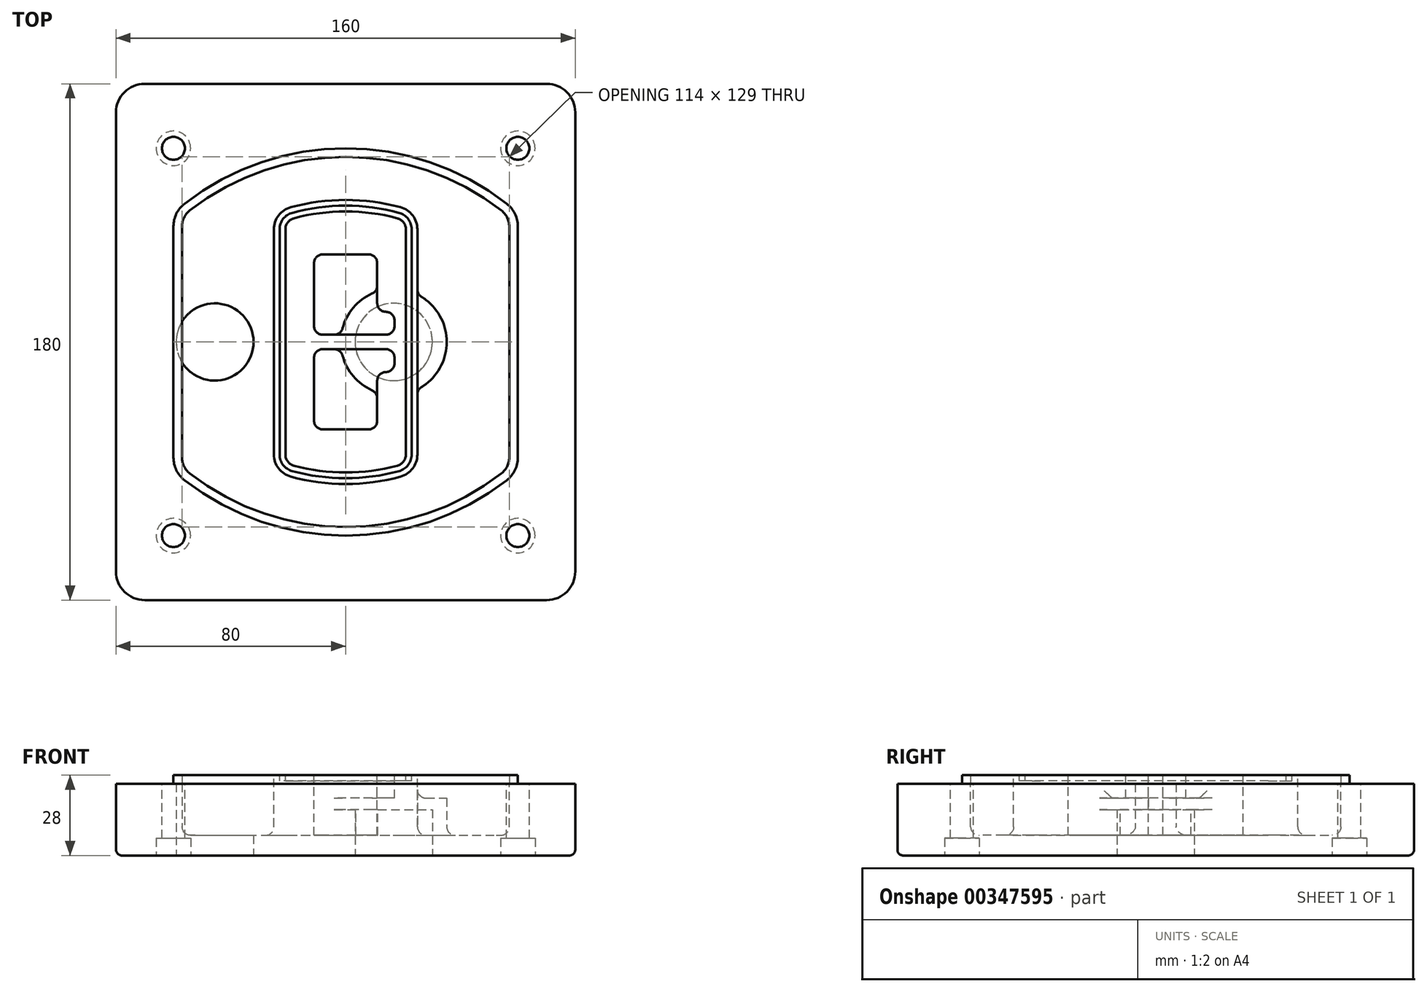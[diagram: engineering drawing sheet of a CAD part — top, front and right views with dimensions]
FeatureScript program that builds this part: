
annotation { "Feature Type Name" : "Feature", "Feature Type Description" : "" }
export const myFeature = defineFeature(function(context is Context, id is Id, definition is map)
    precondition{}
    {
        {
            var Q0;
            Q0=qCreatedBy(makeId("Top.planeOp"),FACE);
            var sketch = newSketch(context, id + "F0", { "sketchPlane" : qUnion([Q0])});
            skPoint(sketch, "E0.rect.middle", {"position": v(0, 0) * mm});
            skLineSegment(sketch, "E1.bottom", {"start": v(-70, -90) * mm, "end": v(70, -90) * mm});
            skLineSegment(sketch, "E1.top", {"start": v(-70, 90) * mm, "end": v(70, 90) * mm});
            skLineSegment(sketch, "E1.left", {"start": v(-80, -80) * mm, "end": v(-80, 80) * mm});
            skLineSegment(sketch, "E1.right", {"start": v(80, -80) * mm, "end": v(80, 80) * mm});
            skLineSegment(sketch, "E2", {"start": v(-80, 90) * mm, "end": v(80, -90) * mm, "construction": true});
            skLineSegment(sketch, "E3", {"start": v(80, 90) * mm, "end": v(-80, -90) * mm, "construction": true});
            skCircle(sketch, "E4", {"center": v(-60, 67.5) * mm, "radius": 4 * mm});
            skCircle(sketch, "E5", {"center": v(60, 67.5) * mm, "radius": 4 * mm});
            skCircle(sketch, "E6", {"center": v(60, -67.5) * mm, "radius": 4 * mm});
            skCircle(sketch, "E7", {"center": v(-60, -67.5) * mm, "radius": 4 * mm});
            skLineSegment(sketch, "E8", {"start": v(-60, 67.5) * mm, "end": v(60, 67.5) * mm, "construction": true});
            skLineSegment(sketch, "E9", {"start": v(60, 67.5) * mm, "end": v(60, -67.5) * mm, "construction": true});
            skLineSegment(sketch, "E10", {"start": v(60, -67.5) * mm, "end": v(-60, -67.5) * mm, "construction": true});
            skLineSegment(sketch, "E11", {"start": v(-60, -67.5) * mm, "end": v(-60, 67.5) * mm, "construction": true});
            skLineSegment(sketch, "E12", {"start": v(-60, 40.3) * mm, "end": v(-60, -40.3) * mm});
            skLineSegment(sketch, "E13", {"start": v(60, 40.3) * mm, "end": v(60, -40.3) * mm});
            skArc(sketch, "E14", {"start": v(56.15, 48.18) * mm, "mid": v(0, 67.5) * mm, "end": v(-56.15, 48.18) * mm});
            skArc(sketch, "E15", {"start": v(-56.15, -48.18) * mm, "mid": v(0, -67.5) * mm, "end": v(56.15, -48.18) * mm});
            skLineSegment(sketch, "E16", {"start": v(-60, 0) * mm, "end": v(60, 0) * mm, "construction": true});
            skPoint(sketch, "E17.visualSharp", {"position": v(-60, -45) * mm});
            skArc(sketch, "E17.filletArc", {"start": v(-60, -40.3) * mm, "mid": v(-58.99, -44.68) * mm, "end": v(-56.15, -48.18) * mm});
            skPoint(sketch, "E18.visualSharp", {"position": v(-60, 45) * mm});
            skArc(sketch, "E18.filletArc", {"start": v(-56.15, 48.18) * mm, "mid": v(-58.99, 44.68) * mm, "end": v(-60, 40.3) * mm});
            skPoint(sketch, "E19.visualSharp", {"position": v(60, 45) * mm});
            skArc(sketch, "E19.filletArc", {"start": v(60, 40.3) * mm, "mid": v(58.99, 44.68) * mm, "end": v(56.15, 48.18) * mm});
            skPoint(sketch, "E20.visualSharp", {"position": v(60, -45) * mm});
            skArc(sketch, "E20.filletArc", {"start": v(56.15, -48.18) * mm, "mid": v(58.99, -44.68) * mm, "end": v(60, -40.3) * mm});
            skPoint(sketch, "E21.visualSharp", {"position": v(-80, 90) * mm});
            skArc(sketch, "E21.filletArc", {"start": v(-70, 90) * mm, "mid": v(-77.07, 87.07) * mm, "end": v(-80, 80) * mm});
            skPoint(sketch, "E22.visualSharp", {"position": v(80, 90) * mm});
            skArc(sketch, "E22.filletArc", {"start": v(80, 80) * mm, "mid": v(77.07, 87.07) * mm, "end": v(70, 90) * mm});
            skPoint(sketch, "E23.visualSharp", {"position": v(80, -90) * mm});
            skArc(sketch, "E23.filletArc", {"start": v(70, -90) * mm, "mid": v(77.07, -87.07) * mm, "end": v(80, -80) * mm});
            skPoint(sketch, "E24.visualSharp", {"position": v(-80, -90) * mm});
            skArc(sketch, "E24.filletArc", {"start": v(-80, -80) * mm, "mid": v(-77.07, -87.07) * mm, "end": v(-70, -90) * mm});
            skArc(sketch, "E25.0", {"start": v(57, 40.3) * mm, "mid": v(56.3, 43.36) * mm, "end": v(54.3, 45.81) * mm});
            skLineSegment(sketch, "E25.1", {"start": v(57, 40.3) * mm, "end": v(57, -40.3) * mm});
            skArc(sketch, "E25.2", {"start": v(54.3, -45.81) * mm, "mid": v(56.3, -43.36) * mm, "end": v(57, -40.3) * mm});
            skArc(sketch, "E25.3", {"start": v(-54.3, -45.81) * mm, "mid": v(0, -64.5) * mm, "end": v(54.3, -45.81) * mm});
            skArc(sketch, "E25.4", {"start": v(-57, -40.3) * mm, "mid": v(-56.3, -43.36) * mm, "end": v(-54.3, -45.81) * mm});
            skArc(sketch, "E25.5", {"start": v(54.3, 45.81) * mm, "mid": v(0, 64.5) * mm, "end": v(-54.3, 45.81) * mm});
            skLineSegment(sketch, "E25.6", {"start": v(-57, 40.3) * mm, "end": v(-57, -40.3) * mm});
            skArc(sketch, "E25.7", {"start": v(-54.3, 45.81) * mm, "mid": v(-56.3, 43.36) * mm, "end": v(-57, 40.3) * mm});
            skArc(sketch, "E26.0", {"start": v(-58.62, 51.33) * mm, "mid": v(-62.58, 46.43) * mm, "end": v(-64, 40.3) * mm});
            skArc(sketch, "E26.1", {"start": v(58.62, 51.33) * mm, "mid": v(0, 71.5) * mm, "end": v(-58.62, 51.33) * mm});
            skArc(sketch, "E26.2", {"start": v(64, 40.3) * mm, "mid": v(62.58, 46.43) * mm, "end": v(58.62, 51.33) * mm});
            skLineSegment(sketch, "E26.3", {"start": v(64, 40.3) * mm, "end": v(64, -40.3) * mm});
            skArc(sketch, "E26.4", {"start": v(58.62, -51.33) * mm, "mid": v(62.58, -46.43) * mm, "end": v(64, -40.3) * mm});
            skLineSegment(sketch, "E26.5", {"start": v(-64, 40.3) * mm, "end": v(-64, -40.3) * mm});
            skArc(sketch, "E26.6", {"start": v(-58.62, -51.33) * mm, "mid": v(0, -71.5) * mm, "end": v(58.62, -51.33) * mm});
            skArc(sketch, "E26.7", {"start": v(-64, -40.3) * mm, "mid": v(-62.58, -46.43) * mm, "end": v(-58.62, -51.33) * mm});
            skSolve(sketch);
        }
        {
            var Q0;
            Q0=makeQuery(id+"F0.imprint","IMPRINT",FACE,{"disambiguationData":[TD([[makeQuery(id+"F0.imprint","IMPRINT",EDGE,{"derivedFrom":sQuery(id+"F0.wireOp",EDGE,"E1.bottom")}),1.0]])]});
            var Q1;
            Q1=makeQuery(id+"F0.imprint","IMPRINT",FACE,{"disambiguationData":[TD([[makeQuery(id+"F0.imprint","IMPRINT",EDGE,{"derivedFrom":sQuery(id+"F0.wireOp",EDGE,"E12")}),1.0]])]});
            var Q2;
            Q2=makeQuery(id+"F0.imprint","IMPRINT",FACE,{"disambiguationData":[TD([[makeQuery(id+"F0.imprint","IMPRINT",EDGE,{"derivedFrom":sQuery(id+"F0.wireOp",EDGE,"E25.0")}),1.0]])]});
            var Q3;
            Q3=makeQuery(id+"F0.imprint","IMPRINT",FACE,{"disambiguationData":[TD([[makeQuery(id+"F0.imprint","IMPRINT",EDGE,{"derivedFrom":sQuery(id+"F0.wireOp",EDGE,"E12")}),-1.0]])]});
            var Q4;
            Q4 = qSketchRegion(id + "FNM3qNsLkxkgVRk_1", true);
            extrude(context, id + "F1", {"entities" : qUnion([Q0, Q1, Q2, Q3, Q4]), "oppositeDirection" : true, "depth" : 25 * mm});
        }
        {
            var Q0;
            Q0=makeQuery(id+"F0.imprint","IMPRINT",FACE,{"disambiguationData":[TD([[makeQuery(id+"F0.imprint","IMPRINT",EDGE,{"derivedFrom":sQuery(id+"F0.wireOp",EDGE,"E12")}),1.0]])]});
            extrude(context, id + "F2", {"entities" : qUnion([Q0]), "depth" : 3 * mm});
        }
        {
            var Q0;
            Q0=makeQuery(id+"F0.imprint","IMPRINT",FACE,{"disambiguationData":[TD([[makeQuery(id+"F0.imprint","IMPRINT",EDGE,{"derivedFrom":sQuery(id+"F0.wireOp",EDGE,"E25.0")}),1.0]])]});
            extrude(context, id + "F3", {"entities" : qUnion([Q0]), "operationType" : NewBodyOperationType.REMOVE, "oppositeDirection" : true, "depth" : 18 * mm});
        }
        {
            var Q0;
            Q0=makeQuery(id+"F2.opExtrude","CAP_FACE",FACE,{"disambiguationData":[OSD([sQuery(id+"F0.wireOp",EDGE,"E12"),sQuery(id+"F0.wireOp",EDGE,"E13"),sQuery(id+"F0.wireOp",EDGE,"E14"),sQuery(id+"F0.wireOp",EDGE,"E15"),sQuery(id+"F0.wireOp",EDGE,"E17.filletArc"),sQuery(id+"F0.wireOp",EDGE,"E18.filletArc"),sQuery(id+"F0.wireOp",EDGE,"E19.filletArc"),sQuery(id+"F0.wireOp",EDGE,"E20.filletArc"),sQuery(id+"F0.wireOp",EDGE,"E25.0"),sQuery(id+"F0.wireOp",EDGE,"E25.1"),sQuery(id+"F0.wireOp",EDGE,"E25.2"),sQuery(id+"F0.wireOp",EDGE,"E25.3"),sQuery(id+"F0.wireOp",EDGE,"E25.4"),sQuery(id+"F0.wireOp",EDGE,"E25.5"),sQuery(id+"F0.wireOp",EDGE,"E25.6"),sQuery(id+"F0.wireOp",EDGE,"E25.7")])],"isStart":false});
            var sketch = newSketch(context, id + "F4", { "sketchPlane" : qUnion([Q0])});
            skArc(sketch, "E27.0", {"start": v(-19.08, -46.97) * mm, "mid": v(0, -49.5) * mm, "end": v(19.08, -46.97) * mm});
            skArc(sketch, "E28.0", {"start": v(19.08, 46.97) * mm, "mid": v(0, 49.5) * mm, "end": v(-19.08, 46.97) * mm});
            skLineSegment(sketch, "E29", {"start": v(-25, 39.25) * mm, "end": v(-25, -39.25) * mm});
            skLineSegment(sketch, "E30", {"start": v(25, 39.25) * mm, "end": v(25, -39.25) * mm});
            skLineSegment(sketch, "E31", {"start": v(-25, 45.1) * mm, "end": v(25, 45.1) * mm, "construction": true});
            skLineSegment(sketch, "E32", {"start": v(-25, -45.1) * mm, "end": v(25, -45.1) * mm, "construction": true});
            skPoint(sketch, "E33.visualSharp", {"position": v(-25, 45.1) * mm});
            skArc(sketch, "E33.filletArc", {"start": v(-19.08, 46.97) * mm, "mid": v(-23.35, 44.11) * mm, "end": v(-25, 39.25) * mm});
            skPoint(sketch, "E34.visualSharp", {"position": v(25, 45.1) * mm});
            skArc(sketch, "E34.filletArc", {"start": v(25, 39.25) * mm, "mid": v(23.35, 44.11) * mm, "end": v(19.08, 46.97) * mm});
            skPoint(sketch, "E35.visualSharp", {"position": v(25, -45.1) * mm});
            skArc(sketch, "E35.filletArc", {"start": v(19.08, -46.97) * mm, "mid": v(23.35, -44.11) * mm, "end": v(25, -39.25) * mm});
            skPoint(sketch, "E36.visualSharp", {"position": v(-25, -45.1) * mm});
            skArc(sketch, "E36.filletArc", {"start": v(-25, -39.25) * mm, "mid": v(-23.35, -44.11) * mm, "end": v(-19.08, -46.97) * mm});
            skArc(sketch, "E37.0", {"start": v(54.3, 45.81) * mm, "mid": v(0, 64.5) * mm, "end": v(-54.3, 45.81) * mm});
            skArc(sketch, "E37.1", {"start": v(-54.3, 45.81) * mm, "mid": v(-56.3, 43.36) * mm, "end": v(-57, 40.3) * mm});
            skLineSegment(sketch, "E37.2", {"start": v(-57, 40.3) * mm, "end": v(-57, -40.3) * mm});
            skArc(sketch, "E37.3", {"start": v(-57, -40.3) * mm, "mid": v(-56.3, -43.36) * mm, "end": v(-54.3, -45.81) * mm});
            skArc(sketch, "E37.4", {"start": v(-54.3, -45.81) * mm, "mid": v(0, -64.5) * mm, "end": v(54.3, -45.81) * mm});
            skArc(sketch, "E37.5", {"start": v(54.3, -45.81) * mm, "mid": v(56.3, -43.36) * mm, "end": v(57, -40.3) * mm});
            skLineSegment(sketch, "E37.6", {"start": v(57, 40.3) * mm, "end": v(57, -40.3) * mm});
            skArc(sketch, "E37.7", {"start": v(57, 40.3) * mm, "mid": v(56.3, 43.36) * mm, "end": v(54.3, 45.81) * mm});
            skLineSegment(sketch, "E38.0", {"start": v(23, 39.25) * mm, "end": v(23, -39.25) * mm});
            skArc(sketch, "E38.1", {"start": v(18.56, -45.04) * mm, "mid": v(21.76, -42.9) * mm, "end": v(23, -39.25) * mm});
            skArc(sketch, "E38.2", {"start": v(-18.56, -45.04) * mm, "mid": v(0, -47.5) * mm, "end": v(18.56, -45.04) * mm});
            skArc(sketch, "E38.3", {"start": v(-23, -39.25) * mm, "mid": v(-21.76, -42.9) * mm, "end": v(-18.56, -45.04) * mm});
            skLineSegment(sketch, "E38.4", {"start": v(-23, 39.25) * mm, "end": v(-23, -39.25) * mm});
            skArc(sketch, "E38.5", {"start": v(23, 39.25) * mm, "mid": v(21.76, 42.9) * mm, "end": v(18.56, 45.04) * mm});
            skArc(sketch, "E38.6", {"start": v(-18.56, 45.04) * mm, "mid": v(-21.76, 42.9) * mm, "end": v(-23, 39.25) * mm});
            skArc(sketch, "E38.7", {"start": v(18.56, 45.04) * mm, "mid": v(0, 47.5) * mm, "end": v(-18.56, 45.04) * mm});
            skArc(sketch, "E39.0", {"start": v(21, 39.25) * mm, "mid": v(20.18, 41.68) * mm, "end": v(18.04, 43.1) * mm});
            skLineSegment(sketch, "E39.1", {"start": v(21, 39.25) * mm, "end": v(21, -39.25) * mm});
            skArc(sketch, "E39.2", {"start": v(18.04, -43.1) * mm, "mid": v(20.18, -41.68) * mm, "end": v(21, -39.25) * mm});
            skArc(sketch, "E39.3", {"start": v(-18.04, -43.1) * mm, "mid": v(0, -45.5) * mm, "end": v(18.04, -43.1) * mm});
            skArc(sketch, "E39.4", {"start": v(-21, -39.25) * mm, "mid": v(-20.18, -41.68) * mm, "end": v(-18.04, -43.1) * mm});
            skArc(sketch, "E39.5", {"start": v(18.04, 43.1) * mm, "mid": v(0, 45.5) * mm, "end": v(-18.04, 43.1) * mm});
            skLineSegment(sketch, "E39.6", {"start": v(-21, 39.25) * mm, "end": v(-21, -39.25) * mm});
            skArc(sketch, "E39.7", {"start": v(-18.04, 43.1) * mm, "mid": v(-20.18, 41.68) * mm, "end": v(-21, 39.25) * mm});
            skLineSegment(sketch, "E40", {"start": v(-25, 0) * mm, "end": v(25, 0) * mm, "construction": true});
            skLineSegment(sketch, "E41", {"start": v(-11, 5.5) * mm, "end": v(-11, 27.5) * mm});
            skLineSegment(sketch, "E42", {"start": v(-8, 30.5) * mm, "end": v(8, 30.5) * mm});
            skLineSegment(sketch, "E43", {"start": v(11, 27.5) * mm, "end": v(11, 13.5) * mm});
            skLineSegment(sketch, "E44", {"start": v(14, 10.5) * mm, "end": v(14, 10.5) * mm});
            skLineSegment(sketch, "E45", {"start": v(17, 7.5) * mm, "end": v(17, 5.5) * mm});
            skLineSegment(sketch, "E46", {"start": v(14, 2.5) * mm, "end": v(-8, 2.5) * mm});
            skPoint(sketch, "E47.visualSharp", {"position": v(-11, 30.5) * mm});
            skArc(sketch, "E47.filletArc", {"start": v(-8, 30.5) * mm, "mid": v(-10.12, 29.62) * mm, "end": v(-11, 27.5) * mm});
            skPoint(sketch, "E48.visualSharp", {"position": v(11, 30.5) * mm});
            skArc(sketch, "E48.filletArc", {"start": v(11, 27.5) * mm, "mid": v(10.12, 29.62) * mm, "end": v(8, 30.5) * mm});
            skPoint(sketch, "E49.visualSharp", {"position": v(11, 10.5) * mm});
            skArc(sketch, "E49.filletArc", {"start": v(11, 13.5) * mm, "mid": v(11.88, 11.38) * mm, "end": v(14, 10.5) * mm});
            skPoint(sketch, "E50.visualSharp", {"position": v(17, 10.5) * mm});
            skArc(sketch, "E50.filletArc", {"start": v(17, 7.5) * mm, "mid": v(16.12, 9.62) * mm, "end": v(14, 10.5) * mm});
            skPoint(sketch, "E51.visualSharp", {"position": v(17, 2.5) * mm});
            skArc(sketch, "E51.filletArc", {"start": v(14, 2.5) * mm, "mid": v(16.12, 3.38) * mm, "end": v(17, 5.5) * mm});
            skPoint(sketch, "E52.visualSharp", {"position": v(-11, 2.5) * mm});
            skArc(sketch, "E52.filletArc", {"start": v(-11, 5.5) * mm, "mid": v(-10.12, 3.38) * mm, "end": v(-8, 2.5) * mm});
            skLineSegment(sketch, "E53.0.MirrorCS", {"start": v(14, -2.5) * mm, "end": v(-8, -2.5) * mm});
            skArc(sketch, "E54.0.MirrorCS", {"start": v(-11, -5.5) * mm, "mid": v(-10.12, -3.38) * mm, "end": v(-8, -2.5) * mm});
            skLineSegment(sketch, "E55.0.MirrorCS", {"start": v(-11, -5.5) * mm, "end": v(-11, -27.5) * mm});
            skArc(sketch, "E56.0.MirrorCS", {"start": v(-8, -30.5) * mm, "mid": v(-10.12, -29.62) * mm, "end": v(-11, -27.5) * mm});
            skLineSegment(sketch, "E57.0.MirrorCS", {"start": v(-8, -30.5) * mm, "end": v(8, -30.5) * mm});
            skArc(sketch, "E58.0.MirrorCS", {"start": v(11, -27.5) * mm, "mid": v(10.12, -29.62) * mm, "end": v(8, -30.5) * mm});
            skLineSegment(sketch, "E59.0.MirrorCS", {"start": v(11, -27.5) * mm, "end": v(11, -13.5) * mm});
            skArc(sketch, "E60.0.MirrorCS", {"start": v(11, -13.5) * mm, "mid": v(11.88, -11.38) * mm, "end": v(14, -10.5) * mm});
            skArc(sketch, "E61.0.MirrorCS", {"start": v(17, -7.5) * mm, "mid": v(16.12, -9.62) * mm, "end": v(14, -10.5) * mm});
            skLineSegment(sketch, "E62.0.MirrorCS", {"start": v(17, -7.5) * mm, "end": v(17, -5.5) * mm});
            skArc(sketch, "E63.0.MirrorCS", {"start": v(14, -2.5) * mm, "mid": v(16.12, -3.38) * mm, "end": v(17, -5.5) * mm});
            skSolve(sketch);
        }
        {
            var Q0;
            Q0=makeQuery(id+"F4.imprint","IMPRINT",FACE,{"disambiguationData":[TD([[makeQuery(id+"F4.imprint","IMPRINT",EDGE,{"derivedFrom":sQuery(id+"F4.wireOp",EDGE,"E27.0")}),1.0]])]});
            var Q1;
            Q1=makeQuery(id+"F4.imprint","IMPRINT",FACE,{"disambiguationData":[TD([[makeQuery(id+"F4.imprint","IMPRINT",EDGE,{"derivedFrom":sQuery(id+"F4.wireOp",EDGE,"E38.0")}),-1.0]])]});
            var Q2;
            Q2=makeQuery(id+"F4.imprint","IMPRINT",FACE,{"disambiguationData":[TD([[makeQuery(id+"F4.imprint","IMPRINT",EDGE,{"derivedFrom":sQuery(id+"F4.wireOp",EDGE,"E39.0")}),1.0]])]});
            extrude(context, id + "F5", {"entities" : qUnion([Q0, Q1, Q2]), "operationType" : NewBodyOperationType.ADD, "endBound" : BoundingType.UP_TO_NEXT, "oppositeDirection" : true, "depth" : 25 * mm});
        }
        {
            var Q0;
            Q0=makeQuery(id+"F4.imprint","IMPRINT",FACE,{"disambiguationData":[TD([[makeQuery(id+"F4.imprint","IMPRINT",EDGE,{"derivedFrom":sQuery(id+"F4.wireOp",EDGE,"E38.0")}),-1.0]])]});
            extrude(context, id + "F6", {"entities" : qUnion([Q0]), "operationType" : NewBodyOperationType.REMOVE, "oppositeDirection" : true, "depth" : 2 * mm});
        }
        {
            var Q0;
            Q0=makeQuery(id+"F1.opExtrude","CAP_FACE",FACE,{"disambiguationData":[OSD([sQuery(id+"F0.wireOp",EDGE,"E1.bottom"),sQuery(id+"F0.wireOp",EDGE,"E1.top"),sQuery(id+"F0.wireOp",EDGE,"E1.left"),sQuery(id+"F0.wireOp",EDGE,"E1.right"),sQuery(id+"F0.wireOp",EDGE,"E4"),sQuery(id+"F0.wireOp",EDGE,"E5"),sQuery(id+"F0.wireOp",EDGE,"E6"),sQuery(id+"F0.wireOp",EDGE,"E7"),sQuery(id+"F0.wireOp",EDGE,"E21.filletArc"),sQuery(id+"F0.wireOp",EDGE,"E22.filletArc"),sQuery(id+"F0.wireOp",EDGE,"E23.filletArc"),sQuery(id+"F0.wireOp",EDGE,"E24.filletArc")])],"isStart":false});
            var sketch = newSketch(context, id + "F7", { "sketchPlane" : qUnion([Q0])});
            skCircle(sketch, "E64", {"center": v(16.76, 0) * mm, "radius": 13.47 * mm});
            skCircle(sketch, "E65", {"center": v(-45.56, 0) * mm, "radius": 13.47 * mm});
            skLineSegment(sketch, "E66", {"start": v(80, 0) * mm, "end": v(-80, 0) * mm});
            skCircle(sketch, "E67", {"center": v(16.76, 0) * mm, "radius": 18.47 * mm});
            skCircle(sketch, "E68", {"center": v(60, -67.5) * mm, "radius": 6 * mm});
            skCircle(sketch, "E69", {"center": v(-60, -67.5) * mm, "radius": 6 * mm});
            skCircle(sketch, "E70", {"center": v(-60, 67.5) * mm, "radius": 6 * mm});
            skCircle(sketch, "E71", {"center": v(60, 67.5) * mm, "radius": 6 * mm});
            skSolve(sketch);
        }
        {
            var Q0;
            {var subQ1=sQuery(id+"F7.wireOp",EDGE,"E66");var subQ4=sQuery(id+"F7.wireOp",EDGE,"E64");var subQ6=makeQuery(id+"F7.imprint","INTERSECT",VERTEX,{"disambiguationData":[OD(0.0)],"derivedFrom":[subQ4,subQ1]});Q0=makeQuery(id+"F7.imprint","IMPRINT",FACE,{"disambiguationData":[TD([[makeQuery(id+"F7.imprint","IMPRINT",EDGE,{"disambiguationData":[TD([[subQ6,-1.0]])],"derivedFrom":subQ4}),-1.0]])]});}
            var Q1;
            {var subQ0=sQuery(id+"F7.wireOp",EDGE,"E66");var subQ1=sQuery(id+"F7.wireOp",EDGE,"E64");var subQ3=makeQuery(id+"F7.imprint","INTERSECT",VERTEX,{"disambiguationData":[OD(0.0)],"derivedFrom":[subQ1,subQ0]});Q1=makeQuery(id+"F7.imprint","IMPRINT",FACE,{"disambiguationData":[TD([[makeQuery(id+"F7.imprint","IMPRINT",EDGE,{"disambiguationData":[TD([[subQ3,-1.0]])],"derivedFrom":subQ1}),1.0]])]});}
            var Q2;
            {var subQ0=sQuery(id+"F7.wireOp",EDGE,"E66");var subQ1=sQuery(id+"F7.wireOp",EDGE,"E64");var subQ3=makeQuery(id+"F7.imprint","INTERSECT",VERTEX,{"disambiguationData":[OD(0.0)],"derivedFrom":[subQ1,subQ0]});Q2=makeQuery(id+"F7.imprint","IMPRINT",FACE,{"disambiguationData":[TD([[makeQuery(id+"F7.imprint","IMPRINT",EDGE,{"disambiguationData":[TD([[subQ3,1.0]])],"derivedFrom":subQ1}),1.0]])]});}
            var Q3;
            {var subQ1=sQuery(id+"F7.wireOp",EDGE,"E66");var subQ4=sQuery(id+"F7.wireOp",EDGE,"E64");var subQ6=makeQuery(id+"F7.imprint","INTERSECT",VERTEX,{"disambiguationData":[OD(0.0)],"derivedFrom":[subQ4,subQ1]});Q3=makeQuery(id+"F7.imprint","IMPRINT",FACE,{"disambiguationData":[TD([[makeQuery(id+"F7.imprint","IMPRINT",EDGE,{"disambiguationData":[TD([[subQ6,1.0]])],"derivedFrom":subQ4}),-1.0]])]});}
            extrude(context, id + "F8", {"entities" : qUnion([Q0, Q1, Q2, Q3]), "operationType" : NewBodyOperationType.ADD, "oppositeDirection" : true, "depth" : 20 * mm});
        }
        {
            var Q0;
            {var subQ0=sQuery(id+"F7.wireOp",EDGE,"E66");var subQ1=sQuery(id+"F7.wireOp",EDGE,"E64");var subQ3=makeQuery(id+"F7.imprint","INTERSECT",VERTEX,{"disambiguationData":[OD(0.0)],"derivedFrom":[subQ1,subQ0]});Q0=makeQuery(id+"F7.imprint","IMPRINT",FACE,{"disambiguationData":[TD([[makeQuery(id+"F7.imprint","IMPRINT",EDGE,{"disambiguationData":[TD([[subQ3,-1.0]])],"derivedFrom":subQ1}),1.0]])]});}
            var Q1;
            {var subQ0=sQuery(id+"F7.wireOp",EDGE,"E66");var subQ1=sQuery(id+"F7.wireOp",EDGE,"E64");var subQ3=makeQuery(id+"F7.imprint","INTERSECT",VERTEX,{"disambiguationData":[OD(0.0)],"derivedFrom":[subQ1,subQ0]});Q1=makeQuery(id+"F7.imprint","IMPRINT",FACE,{"disambiguationData":[TD([[makeQuery(id+"F7.imprint","IMPRINT",EDGE,{"disambiguationData":[TD([[subQ3,1.0]])],"derivedFrom":subQ1}),1.0]])]});}
            extrude(context, id + "F9", {"entities" : qUnion([Q0, Q1]), "operationType" : NewBodyOperationType.REMOVE, "oppositeDirection" : true, "depth" : 16 * mm});
        }
        {
            var Q0;
            {var subQ0=sQuery(id+"F7.wireOp",EDGE,"E66");var subQ1=sQuery(id+"F7.wireOp",EDGE,"E65");var subQ3=makeQuery(id+"F7.imprint","INTERSECT",VERTEX,{"disambiguationData":[OD(0.0)],"derivedFrom":[subQ1,subQ0]});Q0=makeQuery(id+"F7.imprint","IMPRINT",FACE,{"disambiguationData":[TD([[makeQuery(id+"F7.imprint","IMPRINT",EDGE,{"disambiguationData":[TD([[subQ3,-1.0]])],"derivedFrom":subQ1}),1.0]])]});}
            var Q1;
            {var subQ0=sQuery(id+"F7.wireOp",EDGE,"E66");var subQ1=sQuery(id+"F7.wireOp",EDGE,"E65");var subQ3=makeQuery(id+"F7.imprint","INTERSECT",VERTEX,{"disambiguationData":[OD(0.0)],"derivedFrom":[subQ1,subQ0]});Q1=makeQuery(id+"F7.imprint","IMPRINT",FACE,{"disambiguationData":[TD([[makeQuery(id+"F7.imprint","IMPRINT",EDGE,{"disambiguationData":[TD([[subQ3,1.0]])],"derivedFrom":subQ1}),1.0]])]});}
            extrude(context, id + "F10", {"entities" : qUnion([Q0, Q1]), "operationType" : NewBodyOperationType.REMOVE, "oppositeDirection" : true, "depth" : 25 * mm});
        }
        {
            var Q0;
            Q0=makeQuery(id+"F7.imprint","IMPRINT",FACE,{"disambiguationData":[TD([[makeQuery(id+"F7.imprint","IMPRINT",EDGE,{"derivedFrom":sQuery(id+"F7.wireOp",EDGE,"E68")}),1.0]])]});
            var Q1;
            Q1=makeQuery(id+"F7.imprint","IMPRINT",FACE,{"disambiguationData":[TD([[makeQuery(id+"F7.imprint","IMPRINT",EDGE,{"derivedFrom":makeQuery(id+"F1.opExtrude","CAP_EDGE",EDGE,{"disambiguationData":[OSD([sQuery(id+"F0.wireOp",EDGE,"E5")])],"isStart":false})}),-1.0]])]});
            var Q2;
            Q2=makeQuery(id+"F7.imprint","IMPRINT",FACE,{"disambiguationData":[TD([[makeQuery(id+"F7.imprint","IMPRINT",EDGE,{"derivedFrom":sQuery(id+"F7.wireOp",EDGE,"E69")}),1.0]])]});
            var Q3;
            Q3=makeQuery(id+"F7.imprint","IMPRINT",FACE,{"disambiguationData":[TD([[makeQuery(id+"F7.imprint","IMPRINT",EDGE,{"derivedFrom":makeQuery(id+"F1.opExtrude","CAP_EDGE",EDGE,{"disambiguationData":[OSD([sQuery(id+"F0.wireOp",EDGE,"E4")])],"isStart":false})}),-1.0]])]});
            var Q4;
            Q4=makeQuery(id+"F7.imprint","IMPRINT",FACE,{"disambiguationData":[TD([[makeQuery(id+"F7.imprint","IMPRINT",EDGE,{"derivedFrom":sQuery(id+"F7.wireOp",EDGE,"E70")}),1.0]])]});
            var Q5;
            Q5=makeQuery(id+"F7.imprint","IMPRINT",FACE,{"disambiguationData":[TD([[makeQuery(id+"F7.imprint","IMPRINT",EDGE,{"derivedFrom":makeQuery(id+"F1.opExtrude","CAP_EDGE",EDGE,{"disambiguationData":[OSD([sQuery(id+"F0.wireOp",EDGE,"E7")])],"isStart":false})}),-1.0]])]});
            var Q6;
            Q6=makeQuery(id+"F7.imprint","IMPRINT",FACE,{"disambiguationData":[TD([[makeQuery(id+"F7.imprint","IMPRINT",EDGE,{"derivedFrom":sQuery(id+"F7.wireOp",EDGE,"E71")}),1.0]])]});
            var Q7;
            Q7=makeQuery(id+"F7.imprint","IMPRINT",FACE,{"disambiguationData":[TD([[makeQuery(id+"F7.imprint","IMPRINT",EDGE,{"derivedFrom":makeQuery(id+"F1.opExtrude","CAP_EDGE",EDGE,{"disambiguationData":[OSD([sQuery(id+"F0.wireOp",EDGE,"E6")])],"isStart":false})}),-1.0]])]});
            extrude(context, id + "F11", {"entities" : qUnion([Q0, Q1, Q2, Q3, Q4, Q5, Q6, Q7]), "operationType" : NewBodyOperationType.REMOVE, "oppositeDirection" : true, "depth" : 6 * mm});
        }
        {
            var Q0;
            Q0=makeQuery(id+"F9.boolean.opBoolean","COPY",FACE,{"derivedFrom":makeQuery(id+"F9.opExtrude","CAP_FACE",FACE,{"disambiguationData":[OSD([sQuery(id+"F7.wireOp",EDGE,"E64")])],"isStart":false})});
            var sketch = newSketch(context, id + "F12", { "sketchPlane" : qUnion([Q0])});
            skArc(sketch, "E72.0", {"start": v(11, 17.55) * mm, "mid": v(2.57, 11.82) * mm, "end": v(-1.54, 2.5) * mm});
            skArc(sketch, "E72.1", {"start": v(-1.54, -2.5) * mm, "mid": v(2.57, -11.82) * mm, "end": v(11, -17.55) * mm});
            skLineSegment(sketch, "E73", {"start": v(-1.54, -2.5) * mm, "end": v(14, -2.5) * mm});
            skLineSegment(sketch, "E74.0", {"start": v(14, 2.5) * mm, "end": v(-1.54, 2.5) * mm});
            skArc(sketch, "E74.1", {"start": v(14, 2.5) * mm, "mid": v(16.12, 3.38) * mm, "end": v(17, 5.5) * mm});
            skLineSegment(sketch, "E74.2", {"start": v(17, 7.5) * mm, "end": v(17, 5.5) * mm});
            skArc(sketch, "E74.3", {"start": v(17, 7.5) * mm, "mid": v(16.12, 9.62) * mm, "end": v(14, 10.5) * mm});
            skArc(sketch, "E74.4", {"start": v(11, 13.5) * mm, "mid": v(11.88, 11.38) * mm, "end": v(14, 10.5) * mm});
            skLineSegment(sketch, "E74.5", {"start": v(11, 17.55) * mm, "end": v(11, 13.5) * mm});
            skLineSegment(sketch, "E74.7", {"start": v(14, -2.5) * mm, "end": v(-1.54, -2.5) * mm});
            skArc(sketch, "E74.8", {"start": v(14, -2.5) * mm, "mid": v(16.12, -3.38) * mm, "end": v(17, -5.5) * mm});
            skLineSegment(sketch, "E74.9", {"start": v(17, -7.5) * mm, "end": v(17, -5.5) * mm});
            skArc(sketch, "E74.10", {"start": v(17, -7.5) * mm, "mid": v(16.12, -9.62) * mm, "end": v(14, -10.5) * mm});
            skArc(sketch, "E74.11", {"start": v(11, -13.5) * mm, "mid": v(11.88, -11.38) * mm, "end": v(14, -10.5) * mm});
            skLineSegment(sketch, "E74.12", {"start": v(11, -17.55) * mm, "end": v(11, -13.5) * mm});
            skPoint(sketch, "E75.orphan", {"position": v(11, -27.5) * mm});
            skPoint(sketch, "E76.orphan", {"position": v(-8, -2.5) * mm});
            skPoint(sketch, "E77.orphan", {"position": v(-8, 2.5) * mm});
            skPoint(sketch, "E78.orphan", {"position": v(11, 27.5) * mm});
            skSolve(sketch);
        }
        {
            var Q0;
            {var subQ7=sQuery(id+"F12.wireOp",EDGE,"E72.0");var subQ14=sQuery(id+"F12.wireOp",EDGE,"E72.1");var subQ16=sQuery(id+"F12.wireOp",EDGE,"E74.1");var subQ18=sQuery(id+"F12.wireOp",EDGE,"E74.8");Q0=qUnion([makeQuery(id+"F12.imprint","IMPRINT",FACE,{"disambiguationData":[TD([[makeQuery(id+"F12.imprint","IMPRINT",EDGE,{"derivedFrom":subQ7}),1.0]])]}),makeQuery(id+"F12.imprint","IMPRINT",FACE,{"disambiguationData":[TD([[makeQuery(id+"F12.imprint","IMPRINT",EDGE,{"derivedFrom":subQ14}),1.0]])]}),makeQuery(id+"F12.imprint","IMPRINT",FACE,{"disambiguationData":[TD([[makeQuery(id+"F12.imprint","IMPRINT",EDGE,{"derivedFrom":subQ16}),1.0]])]}),makeQuery(id+"F12.imprint","IMPRINT",FACE,{"disambiguationData":[TD([[makeQuery(id+"F12.imprint","IMPRINT",EDGE,{"derivedFrom":subQ18}),-1.0]])]})]);}
            var Q1;
            Q1=makeQuery(id+"F5.boolean.opBoolean","SPLIT",FACE,{"disambiguationData":[TD([makeQuery(id+"F5.opExtrude","SWEPT_FACE",FACE,{"disambiguationData":[OSD([sQuery(id+"F4.wireOp",EDGE,"E41")])]})])],"derivedFrom":makeQuery(id+"F3.boolean.opBoolean","COPY",FACE,{"derivedFrom":makeQuery(id+"F3.opExtrude","CAP_FACE",FACE,{"disambiguationData":[OSD([sQuery(id+"F0.wireOp",EDGE,"E25.0"),sQuery(id+"F0.wireOp",EDGE,"E25.1"),sQuery(id+"F0.wireOp",EDGE,"E25.2"),sQuery(id+"F0.wireOp",EDGE,"E25.3"),sQuery(id+"F0.wireOp",EDGE,"E25.4"),sQuery(id+"F0.wireOp",EDGE,"E25.5"),sQuery(id+"F0.wireOp",EDGE,"E25.6"),sQuery(id+"F0.wireOp",EDGE,"E25.7")])],"isStart":false})})});
            extrude(context, id + "F13", {"entities" : qUnion([Q0]), "operationType" : NewBodyOperationType.REMOVE, "endBound" : BoundingType.UP_TO_SURFACE, "endBoundEntityFace" : qUnion([Q1]), "depth" : 25 * mm});
        }
        {
            var Q0;
            Q0=makeQuery(id+"F3.boolean.opBoolean","COPY",EDGE,{"derivedFrom":makeQuery(id+"F3.opExtrude","CAP_EDGE",EDGE,{"disambiguationData":[OSD([sQuery(id+"F0.wireOp",EDGE,"E25.6")])],"isStart":false})});
            var Q1;
            Q1=makeQuery(id+"F8.boolean.opBoolean","INTERSECT",EDGE,{"derivedFrom":[makeQuery(id+"F5.opExtrude","SWEPT_FACE",FACE,{"disambiguationData":[OSD([sQuery(id+"F4.wireOp",EDGE,"E30")])]}),makeQuery(id+"F8.opExtrude","CAP_FACE",FACE,{"disambiguationData":[OSD([sQuery(id+"F7.wireOp",EDGE,"E67")])],"isStart":false})]});
            var Q2;
            Q2=makeQuery(id+"F8.boolean.opBoolean","INTERSECT",EDGE,{"disambiguationData":[OD(1.0)],"derivedFrom":[makeQuery(id+"F5.opExtrude","SWEPT_FACE",FACE,{"disambiguationData":[OSD([sQuery(id+"F4.wireOp",EDGE,"E30")])]}),makeQuery(id+"F8.opExtrude","SWEPT_FACE",FACE,{"disambiguationData":[OSD([sQuery(id+"F7.wireOp",EDGE,"E67")])]})]});
            var Q3;
            {var subQ0=sQuery(id+"F4.wireOp",EDGE,"E30");Q3=makeQuery(id+"F8.boolean.opBoolean","SPLIT",EDGE,{"disambiguationData":[TD([makeQuery(id+"F5.opExtrude","SWEPT_FACE",FACE,{"disambiguationData":[OSD([sQuery(id+"F4.wireOp",EDGE,"E35.filletArc")])]})])],"derivedFrom":makeQuery(id+"F5.opExtrude","CAP_EDGE",EDGE,{"disambiguationData":[OSD([subQ0])],"isStart":false})});}
            var Q4;
            {var subQ0=makeQuery(id+"F8.opExtrude","SWEPT_FACE",FACE,{"disambiguationData":[OSD([sQuery(id+"F7.wireOp",EDGE,"E67")])]});var subQ1=makeQuery(id+"F5.opExtrude","SWEPT_FACE",FACE,{"disambiguationData":[OSD([sQuery(id+"F4.wireOp",EDGE,"E30")])]});var subQ2=sQuery(id+"F0.wireOp",EDGE,"E25.3");var subQ3=sQuery(id+"F0.wireOp",EDGE,"E25.7");var subQ4=sQuery(id+"F0.wireOp",EDGE,"E25.6");var subQ5=sQuery(id+"F0.wireOp",EDGE,"E25.5");var subQ6=sQuery(id+"F0.wireOp",EDGE,"E25.4");var subQ7=sQuery(id+"F0.wireOp",EDGE,"E25.0");var subQ8=sQuery(id+"F0.wireOp",EDGE,"E25.1");var subQ9=sQuery(id+"F0.wireOp",EDGE,"E25.2");Q4=qUnion([makeQuery(id+"F8.boolean.opBoolean","INTERSECT",EDGE,{"derivedFrom":[makeQuery(id+"F5.boolean.opBoolean","SPLIT",FACE,{"disambiguationData":[TD([makeQuery(id+"F3.boolean.opBoolean","COPY",FACE,{"derivedFrom":makeQuery(id+"F3.opExtrude","SWEPT_FACE",FACE,{"disambiguationData":[OSD([subQ7])]})})])],"derivedFrom":makeQuery(id+"F3.boolean.opBoolean","COPY",FACE,{"derivedFrom":makeQuery(id+"F3.opExtrude","CAP_FACE",FACE,{"disambiguationData":[OSD([subQ7,subQ8,subQ9,subQ2,subQ6,subQ5,subQ4,subQ3])],"isStart":false})})}),subQ0]}),makeQuery(id+"F8.boolean.opBoolean","INTERSECT",EDGE,{"derivedFrom":[makeQuery(id+"F5.opExtrude","SWEPT_FACE",FACE,{"disambiguationData":[OSD([sQuery(id+"F4.wireOp",EDGE,"E53.0.MirrorCS")])]}),subQ0]}),makeQuery(id+"F8.boolean.opBoolean","INTERSECT",EDGE,{"derivedFrom":[makeQuery(id+"F5.opExtrude","SWEPT_FACE",FACE,{"disambiguationData":[OSD([sQuery(id+"F4.wireOp",EDGE,"E46")])]}),subQ0]}),makeQuery(id+"F8.boolean.opBoolean","INTERSECT",EDGE,{"disambiguationData":[OD(1.0)],"derivedFrom":[subQ1,subQ0]}),makeQuery(id+"F8.boolean.opBoolean","INTERSECT",EDGE,{"derivedFrom":[makeQuery(id+"F5.opExtrude","SWEPT_FACE",FACE,{"disambiguationData":[OSD([sQuery(id+"F4.wireOp",EDGE,"E43")])]}),subQ0]}),makeQuery(id+"F8.boolean.opBoolean","INTERSECT",EDGE,{"disambiguationData":[OD(0.0)],"derivedFrom":[subQ1,subQ0]}),makeQuery(id+"F8.boolean.opBoolean","INTERSECT",EDGE,{"derivedFrom":[makeQuery(id+"F5.opExtrude","SWEPT_FACE",FACE,{"disambiguationData":[OSD([sQuery(id+"F4.wireOp",EDGE,"E59.0.MirrorCS")])]}),subQ0]})]);}
            var Q5;
            Q5=makeQuery(id+"F8.boolean.opBoolean","INTERSECT",EDGE,{"disambiguationData":[OD(0.0)],"derivedFrom":[makeQuery(id+"F5.opExtrude","SWEPT_FACE",FACE,{"disambiguationData":[OSD([sQuery(id+"F4.wireOp",EDGE,"E30")])]}),makeQuery(id+"F8.opExtrude","SWEPT_FACE",FACE,{"disambiguationData":[OSD([sQuery(id+"F7.wireOp",EDGE,"E67")])]})]});
            fillet(context, id + "F14", {"entities" : qUnion([Q0, Q1, Q2, Q3, Q4, Q5]), "radius" : 3 * mm, "tangentPropagation" : true, "allowEdgeOverflow" : false});
        }
        {
            var Q0;
            Q0=makeQuery(id+"F1.opExtrude","CAP_EDGE",EDGE,{"disambiguationData":[OSD([sQuery(id+"F0.wireOp",EDGE,"E1.bottom")])],"isStart":false});
            fillet(context, id + "F15", {"entities" : qUnion([Q0]), "radius" : 2 * mm, "tangentPropagation" : true, "allowEdgeOverflow" : false});
        }
    });
